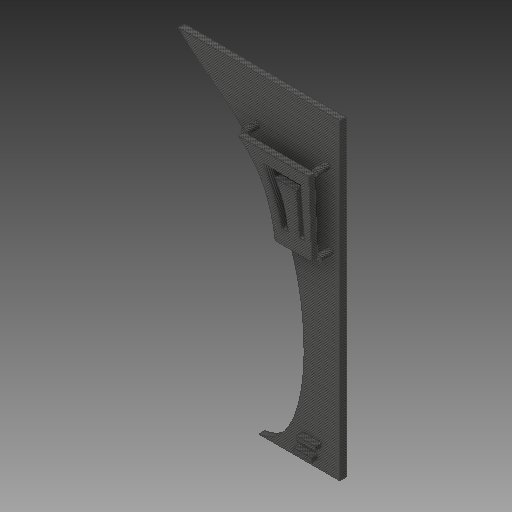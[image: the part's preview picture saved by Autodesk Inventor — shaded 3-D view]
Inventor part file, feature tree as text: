
AUTODESK INVENTOR PART (.ipt)
format: ipt  version: 2018 (Build 220112000, 112)  size: 210,944 bytes
history: native  units: mm
features: extrude x6, sketch x6
ambient origin geometry x8: Origin, YZ Plane, XZ Plane, XY Plane, X Axis, Y Axis, Z Axis, Center Point
bodies: Solid1 (feature_tree)
feature tree (12):
  extrude  "Extrusion1"  Depth=10.0mm
  extrude  "Extrusion2"  Depth=10.0mm
  extrude  "Extrusion3"  Depth=20.0mm TaperAngle=0.0deg
  extrude  "Extrusion4"  Depth=10.0mm
  extrude  "Extrusion6"  Depth=10.0mm TaperAngle=0.0deg
  extrude  "Extrusion8"  Depth=7.0mm
  sketch  "Sketch1"  dims[d3=10.0mm d4=0.0mm d5=10.0mm]
  sketch  "Sketch2"  dims[d6=10.0mm d7=10.0mm]
  sketch  "Sketch3"  dims[d8=10.0mm d9=20.0mm d10=0.0mm]
  sketch  "Sketch4"  dims[d11=10.0mm d12=0.0mm d13=60.0mm]
  sketch  "Sketch6"  dims[d14=74.0mm d15=10.0mm d16=0.0mm]
  sketch  "Sketch8"  dims[d22=30.0mm d23=7.0mm d24=30.0mm d25=7.0mm d26=10.0mm d27=0.0mm d32=10.0mm d33=376.966mm d34=10.0mm d35=10.0mm d36=0.0mm]
